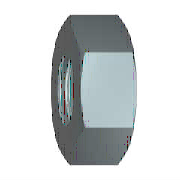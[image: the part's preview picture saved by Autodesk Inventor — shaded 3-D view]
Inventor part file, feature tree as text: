
AUTODESK INVENTOR PART (.ipt)
format: ipt  version: 2024 (Build 280153000, 153)  size: 162,816 bytes
history: native  units: mm (DEFAULTED — no unit token found)
features: other x2, extrude x1, hole x1, plane x1
ambient origin geometry x7: Origin, YZ Plane, XZ Plane, X Axis, Y Axis, Z Axis, Center Point
bodies: Solid1 (feature_tree)
feature tree (5):
  extrude  "Базовый элемент"  Depth=8.082904mm
  other  "Фаска1"
  hole  "Резьба"  [1 undecoded]
  other  "Work Axis1"
  plane  "Work Plane1"
note: 1 required parameter value undecoded (feature->parameter linkage not recoverable at this tier; creation-order binding heuristic only, values carry confidence <= 0.55)
